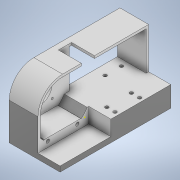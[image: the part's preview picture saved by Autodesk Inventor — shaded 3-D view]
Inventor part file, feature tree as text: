
AUTODESK INVENTOR PART (.ipt)
format: ipt  version: 2022 (Build 260153000, 153)  size: 1,391,616 bytes
history: mixed  units: mm
features: sketch x32, extrude x31, other x3, fillet x1, plane x1, imported_body x1
ambient origin geometry x8: Origin, YZ Plane, XZ Plane, XY Plane, X Axis, Y Axis, Z Axis, Center Point
bodies: Solid1 (imported_parasolid)
feature tree (69):
  other  "Assembly2.iam"
  other  "96Gears_Stage_1_modified.ipt:1"
  other  "96Gears_Stage_2_modified.ipt:1"
  extrude  "Extrusion3"  Depth=3.0mm
  extrude  "Extrusion5"  Depth=18.0mm TaperAngle=0.0deg
  extrude  "Extrusion6"  Depth=6.0mm TaperAngle=0.0deg
  extrude  "Extrusion7"  Depth=10.0mm TaperAngle=0.0deg
  extrude  "Extrusion8"  Depth=4.1mm
  extrude  "Extrusion9"  Depth=7.0mm
  extrude  "Extrusion10"  Depth=50.0mm TaperAngle=0.0deg
  extrude  "Extrusion11"  Depth=50.0mm TaperAngle=0.0deg
  extrude  "Extrusion12"  Depth=3.0mm TaperAngle=0.0deg
  extrude  "Extrusion13"  Depth=3.0mm TaperAngle=0.0deg
  extrude  "Extrusion14"  Depth=3.0mm TaperAngle=0.0deg
  extrude  "Extrusion15"  Depth=9.0mm TaperAngle=0.0deg
  extrude  "Extrusion16"  Depth=30.0mm
  fillet  "Fillet1"  Radius=5.0mm
  extrude  "Extrusion17"  Depth=10.0mm TaperAngle=0.0deg
  extrude  "Extrusion18"  Depth=10.0mm TaperAngle=0.0deg
  extrude  "Extrusion19"  Depth=1.25mm
  extrude  "Extrusion20"  Depth=10.0mm TaperAngle=0.0deg
  extrude  "Extrusion21"  Depth=10.0mm TaperAngle=0.0deg
  extrude  "Extrusion22"  Depth=10.0mm TaperAngle=0.0deg
  plane  "Work Plane1"
  extrude  "Extrusion26"  Depth=10.0mm TaperAngle=0.0deg
  extrude  "Extrusion27"  Depth=10.0mm
  extrude  "Extrusion28"  Depth=10.0mm TaperAngle=0.0deg
  extrude  "Extrusion29"  Depth=10.0mm TaperAngle=0.0deg
  extrude  "Extrusion30"  Depth=25.0mm TaperAngle=0.0deg
  extrude  "Extrusion31"  Depth=25.0mm
  extrude  "Extrusion32"  Depth=4.1mm
  extrude  "Extrusion33"  Depth=25.0mm
  extrude  "Extrusion34"  Depth=4.1mm
  extrude  "Extrusion35"  Depth=10.0mm
  extrude  "Extrusion36"  [1 undecoded]
  extrude  "Extrusion37"  [1 undecoded]
  sketch  "Sketch5"  dims[d7=6.0mm d8=18.0mm d9=0.0mm]
  sketch  "Sketch4"  dims[d0=10.0mm d6=3.0mm]
  sketch  "Sketch7"  dims[d17=32.25mm d18=6.0mm d19=0.0mm]
  sketch  "Sketch8"  dims[d20=10.0mm d21=10.0mm d22=0.0mm]
  sketch  "Sketch9"  dims[d24=4.1mm d25=4.1mm]
  sketch  "Sketch10"  dims[d26=10.0mm d27=0.0mm d28=7.0mm]
  sketch  "Sketch11"  dims[d29=0.0mm d30=0.0mm d31=50.0mm d32=0.0mm]
  sketch  "Sketch12"  dims[d33=3.0mm d34=50.0mm d35=0.0mm]
  sketch  "Sketch13"  dims[d38=3.0mm d39=3.0mm d40=0.0mm]
  sketch  "Sketch14"  dims[d41=23.0mm d42=3.0mm d43=0.0mm]
  sketch  "Sketch15"  dims[d44=3.0mm d45=0.0mm d46=9.0mm d47=0.0mm]
  sketch  "Sketch16"  dims[d49=33.25mm d50=9.0mm d51=0.0mm]
  sketch  "Sketch17"  dims[d52=2.0mm d53=0.0mm d54=30.0mm d55=5.0mm]
  sketch  "Sketch18"  dims[d57=5.0mm d58=10.0mm d59=0.0mm]
  sketch  "Sketch19"  dims[d60=3.0mm d61=10.0mm d62=0.0mm]
  sketch  "Sketch20"  dims[d63=2.0mm d64=0.0mm d65=1.25mm]
  sketch  "Sketch21"  dims[d66=2.0mm d67=0.0mm d68=10.0mm d69=0.0mm]
  sketch  "Sketch22"  dims[d74=2.5mm d75=10.0mm d76=0.0mm]
  sketch  "Sketch23"  dims[d98=10.0mm d99=0.0mm d100=10.0mm d101=0.0mm]
  sketch  "Sketch25"  dims[d102=10.0mm d103=0.0mm d104=10.0mm d105=0.0mm]
  sketch  "Sketch29"  dims[d106=10.0mm d107=0.0mm d108=8.0mm]
  sketch  "Sketch30"  dims[d109=16.0mm d110=10.0mm d111=0.0mm]
  sketch  "Sketch31"  dims[d112=2.5mm d114=10.0mm d115=0.0mm]
  sketch  "Sketch32"  dims[d116=10.0mm d117=0.0mm d118=25.0mm d119=0.0mm]
  sketch  "Sketch33"  dims[d120=25.0mm d121=0.0mm d122=12.5mm]
  sketch  "Sketch34"  dims[d123=1.5mm d124=4.1mm]
  sketch  "Sketch35"  dims[d125=0.0mm d126=0.0mm d128=25.0mm]
  sketch  "Sketch36"  dims[d129=12.865mm d133=4.1mm]
  sketch  "Sketch37"  dims[d134=10.0mm d135=0.0mm d136=4.1mm]
  sketch  "Sketch38"
  sketch  "Sketch39"
  sketch  "Sketch40"
  imported_body  NMx_Import_Brep_tag  [imported B-rep: ~46 faces, bbox_mm=[62.0, 75.0, 135.0]]
note: 2 required parameter values undecoded (feature->parameter linkage not recoverable at this tier; creation-order binding heuristic only, values carry confidence <= 0.55)
